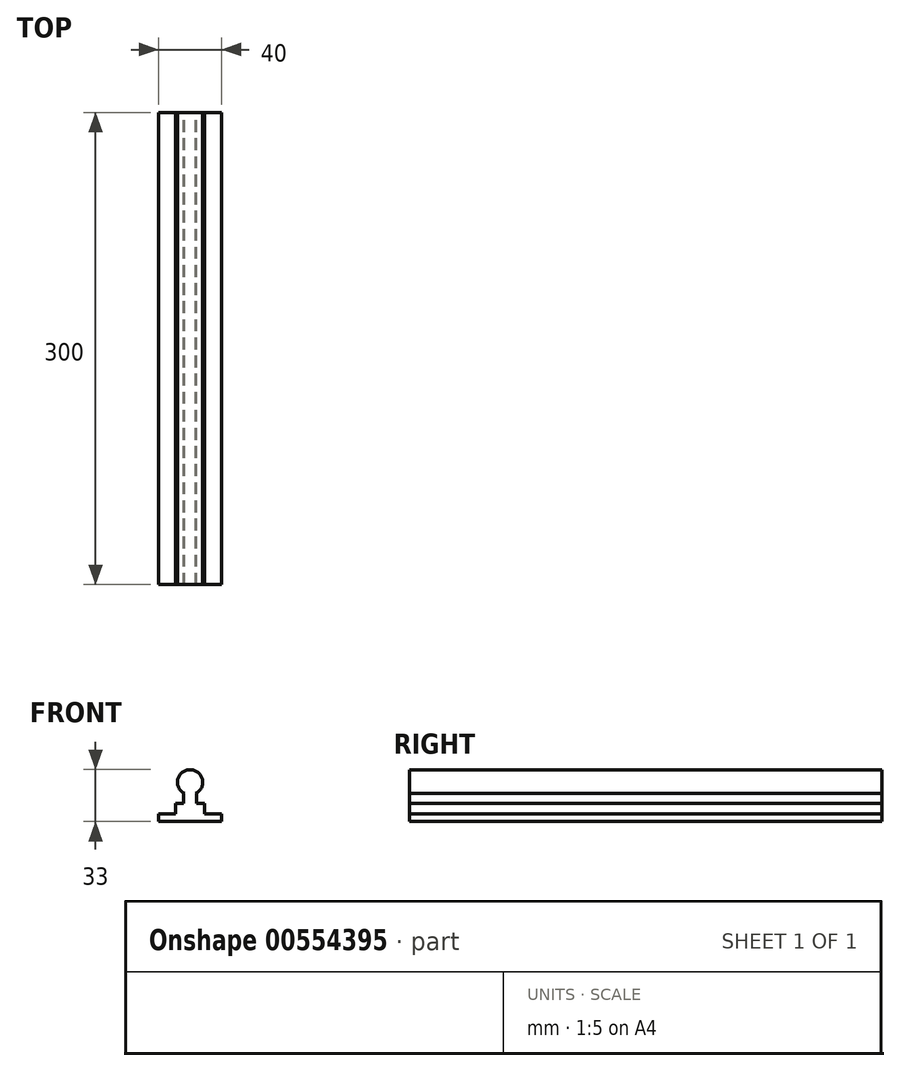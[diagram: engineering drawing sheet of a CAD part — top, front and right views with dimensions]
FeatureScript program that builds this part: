
annotation { "Feature Type Name" : "Feature", "Feature Type Description" : "" }
export const myFeature = defineFeature(function(context is Context, id is Id, definition is map)
    precondition{}
    {
        {
            var Q0;
            Q0=qCreatedBy(makeId("Front.planeOp"),FACE);
            var sketch = newSketch(context, id + "F0", { "sketchPlane" : qUnion([Q0])});
            skLineSegment(sketch, "E0.bottom", {"start": v(-34, -10.6) * mm, "end": v(6, -10.6) * mm});
            skLineSegment(sketch, "E0.top", {"start": v(-34, -5.6) * mm, "end": v(-23.24, -5.6) * mm});
            skLineSegment(sketch, "E0.left", {"start": v(-34, -10.6) * mm, "end": v(-34, -5.6) * mm});
            skLineSegment(sketch, "E0.right", {"start": v(6, -10.6) * mm, "end": v(6, -5.6) * mm});
            skArc(sketch, "E1", {"start": v(-10.5, 7.2) * mm, "mid": v(-14, 22.4) * mm, "end": v(-17.48, 7.2) * mm});
            skLineSegment(sketch, "E2.top", {"start": v(-23.24, 1.05) * mm, "end": v(-18, 1.05) * mm});
            skLineSegment(sketch, "E2.left", {"start": v(-23.24, -5.6) * mm, "end": v(-23.24, 1.05) * mm});
            skLineSegment(sketch, "E2.right", {"start": v(-4.74, -5.6) * mm, "end": v(-4.74, 1.05) * mm});
            skLineSegment(sketch, "E3", {"start": v(-14, 1.05) * mm, "end": v(-14, -5.6) * mm, "construction": true});
            skLineSegment(sketch, "E4.top", {"start": v(-18, 7.2) * mm, "end": v(-17.48, 7.2) * mm});
            skLineSegment(sketch, "E4.left", {"start": v(-18, 1.05) * mm, "end": v(-18, 7.2) * mm});
            skLineSegment(sketch, "E4.right", {"start": v(-10, 1.05) * mm, "end": v(-10, 7.2) * mm});
            skLineSegment(sketch, "E5.bottom", {"start": v(-14, 7.2) * mm, "end": v(-14, 7.2) * mm});
            skLineSegment(sketch, "E5.top", {"start": v(-14, 1.05) * mm, "end": v(-14, 1.05) * mm});
            skLineSegment(sketch, "E5.right", {"start": v(-14, 7.2) * mm, "end": v(-14, 1.05) * mm, "construction": true});
            skLineSegment(sketch, "E6.trimOffspring", {"start": v(-10, 1.05) * mm, "end": v(-4.74, 1.05) * mm});
            skLineSegment(sketch, "E7.trimOffspring", {"start": v(-4.74, -5.6) * mm, "end": v(6, -5.6) * mm});
            skLineSegment(sketch, "E8.trimOffspring", {"start": v(-10.5, 7.2) * mm, "end": v(-10, 7.2) * mm});
            skSolve(sketch);
        }
        {
            var Q0;
            Q0=makeQuery(id+"F0.imprint","IMPRINT",FACE,{"disambiguationData":[TD([[makeQuery(id+"F0.imprint","IMPRINT",EDGE,{"derivedFrom":sQuery(id+"F0.wireOp",EDGE,"E0.bottom")}),1.0]])]});
            extrude(context, id + "F1", {"entities" : qUnion([Q0]), "depth" : 300 * mm, "offsetDistance" : 25 * mm});
        }
    });
